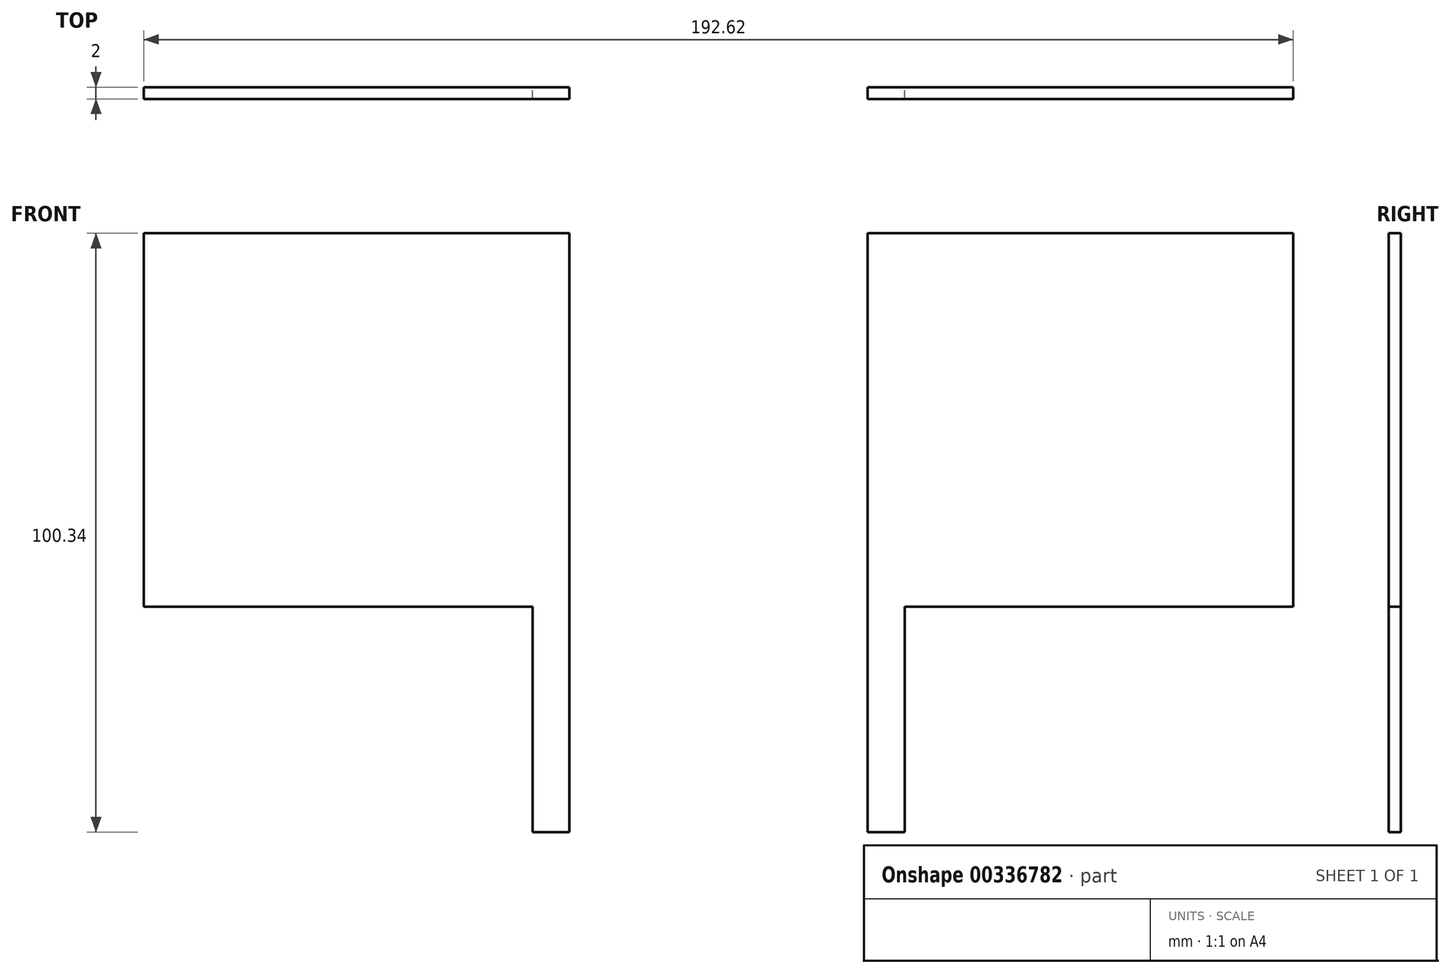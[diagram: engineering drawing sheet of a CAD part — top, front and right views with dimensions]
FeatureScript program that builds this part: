
annotation { "Feature Type Name" : "Feature", "Feature Type Description" : "" }
export const myFeature = defineFeature(function(context is Context, id is Id, definition is map)
    precondition{}
    {
        {
            var Q0;
            Q0=qCreatedBy(makeId("Front.planeOp"),FACE);
            var sketch = newSketch(context, id + "F0", { "sketchPlane" : qUnion([Q0])});
            skLineSegment(sketch, "E0.bottom", {"start": v(0, 62.6) * mm, "end": v(-71.31, 62.6) * mm});
            skLineSegment(sketch, "E0.top", {"start": v(-6.17, 0) * mm, "end": v(-71.31, 0) * mm});
            skLineSegment(sketch, "E0.left", {"start": v(0, 62.6) * mm, "end": v(0, 0) * mm});
            skLineSegment(sketch, "E0.right", {"start": v(-71.31, 62.6) * mm, "end": v(-71.31, 0) * mm});
            skLineSegment(sketch, "E1.top", {"start": v(0, -37.74) * mm, "end": v(-6.17, -37.74) * mm});
            skLineSegment(sketch, "E1.left", {"start": v(0, 0) * mm, "end": v(0, -37.74) * mm});
            skLineSegment(sketch, "E2", {"start": v(-6.17, 0) * mm, "end": v(-6.17, -37.74) * mm});
            skSolve(sketch);
        }
        {
            var Q0;
            Q0=makeQuery(id+"F0.imprint","IMPRINT",FACE,{"disambiguationData":[TD([[makeQuery(id+"F0.imprint","IMPRINT",EDGE,{"derivedFrom":sQuery(id+"F0.wireOp",EDGE,"E0.bottom")}),1.0]])]});
            extrude(context, id + "F1", {"entities" : qUnion([Q0]), "depth" : 2 * mm});
        }
        {
            var Q0;
            Q0=qCreatedBy(makeId("Right.planeOp"),FACE);
            cPlane(context, id + "F2", {"entities" : qUnion([Q0]), "cplaneType" : CPlaneType.OFFSET, "offset" : 25 * mm, "width" : 150 * mm, "height" : 150 * mm});
        }
        {
            var Q0;
            Q0=makeQuery(id+"F1.opExtrude","SWEPT_BODY",BODY,{"disambiguationData":[OSD([sQuery(id+"F0.wireOp",EDGE,"E0.bottom"),sQuery(id+"F0.wireOp",EDGE,"E0.top"),sQuery(id+"F0.wireOp",EDGE,"E0.left"),sQuery(id+"F0.wireOp",EDGE,"E0.right"),sQuery(id+"F0.wireOp",EDGE,"E1.top"),sQuery(id+"F0.wireOp",EDGE,"E1.left"),sQuery(id+"F0.wireOp",EDGE,"E2")])]});
            var Q1;
            Q1=qCreatedBy(id+"F2.planeOp",FACE);
            mirror(context, id + "F3", {"entities" : qUnion([Q0]), "mirrorPlane" : qUnion([Q1])});
        }
    });
